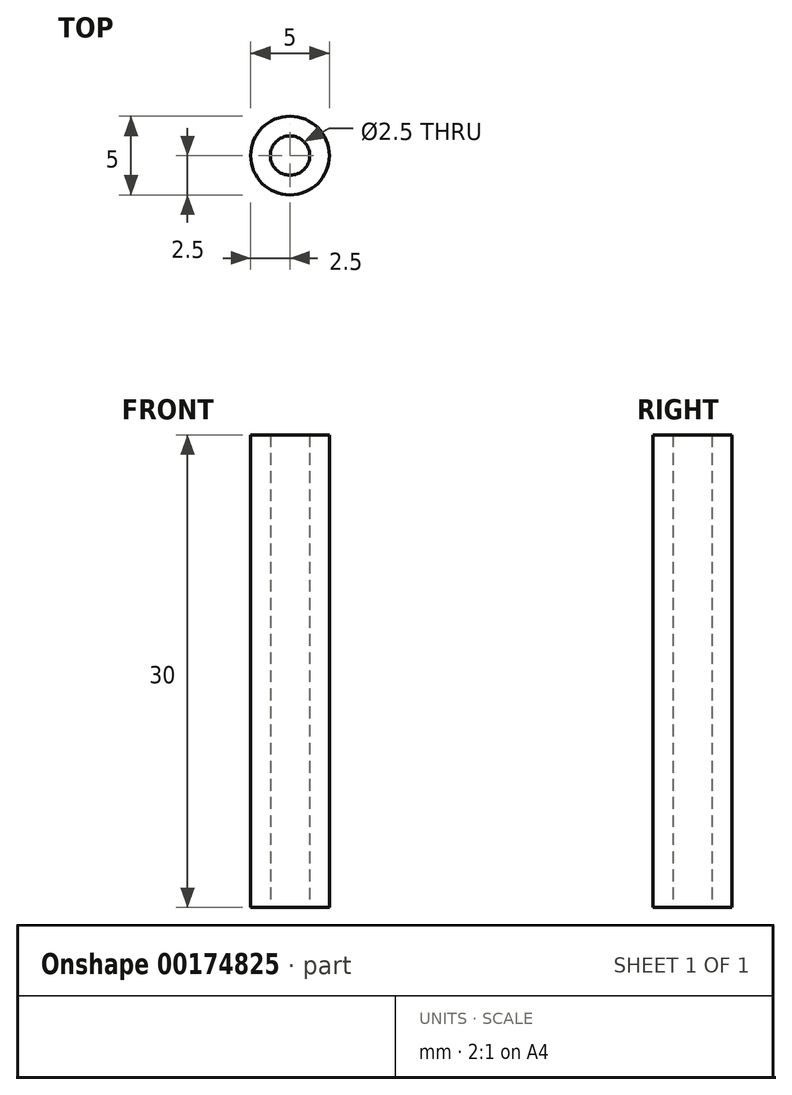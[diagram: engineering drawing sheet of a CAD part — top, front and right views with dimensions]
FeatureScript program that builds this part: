
annotation { "Feature Type Name" : "Feature", "Feature Type Description" : "" }
export const myFeature = defineFeature(function(context is Context, id is Id, definition is map)
    precondition{}
    {
        {
            var Q0;
            Q0=qCreatedBy(makeId("Top.planeOp"),FACE);
            var sketch = newSketch(context, id + "F0", { "sketchPlane" : qUnion([Q0])});
            skCircle(sketch, "E0", {"center": v(0, 0) * mm, "radius": 2.5 * mm});
            skCircle(sketch, "E1", {"center": v(0, 0) * mm, "radius": 1.25 * mm});
            skSolve(sketch);
        }
        {
            var Q0;
            Q0 = qSketchRegion(id + "F0", true);
            extrude(context, id + "F1", {"entities" : qUnion([Q0]), "depth" : 30 * mm});
        }
    });
